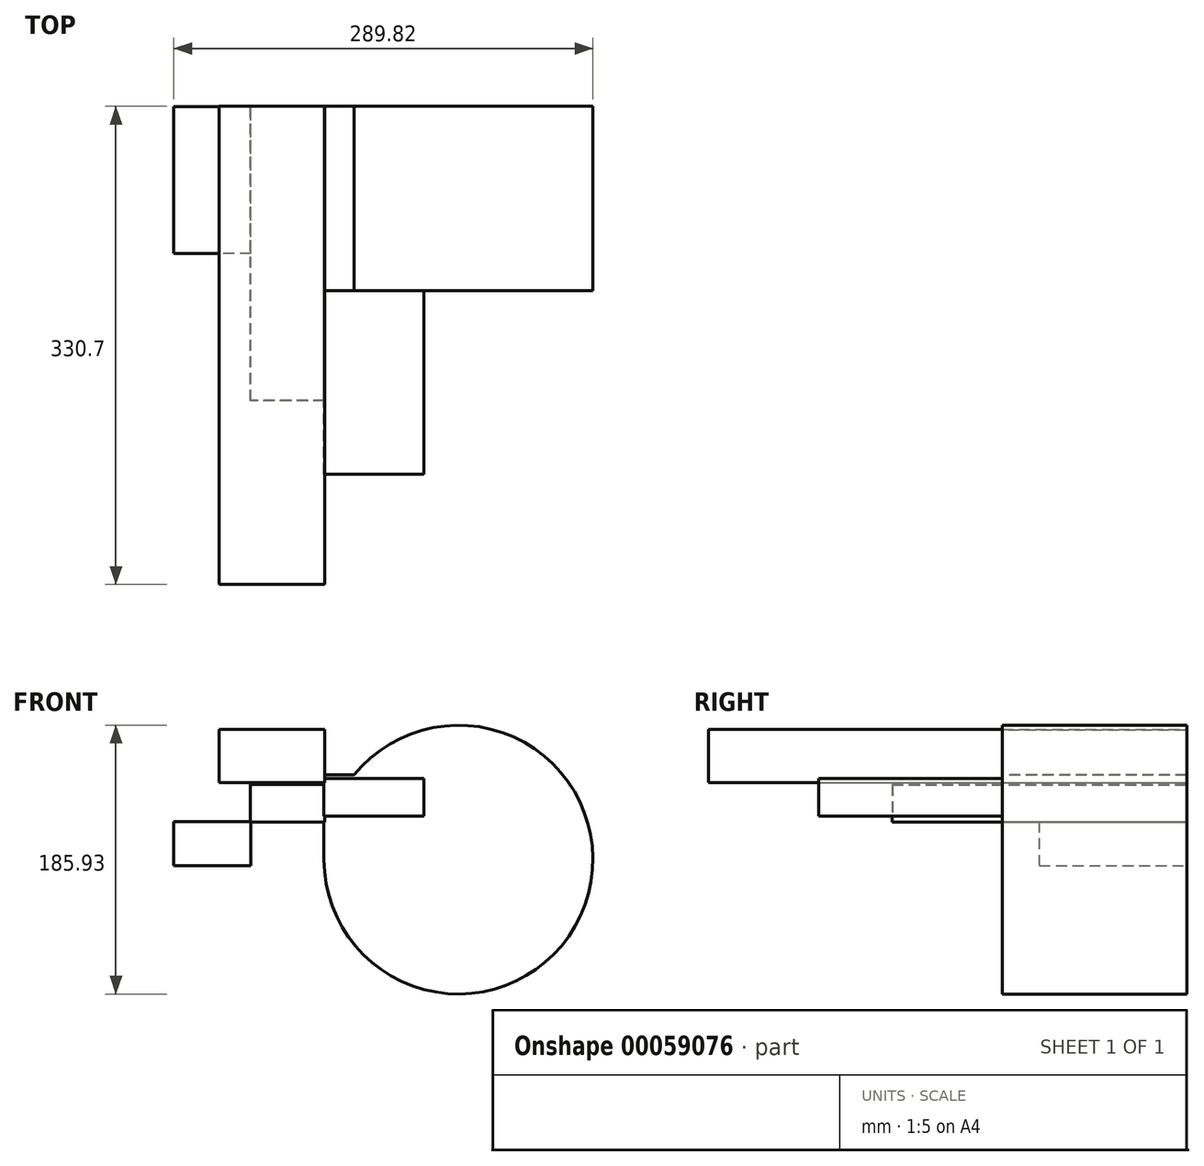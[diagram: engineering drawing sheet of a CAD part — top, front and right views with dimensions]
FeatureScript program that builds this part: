
annotation { "Feature Type Name" : "Feature", "Feature Type Description" : "" }
export const myFeature = defineFeature(function(context is Context, id is Id, definition is map)
    precondition{}
    {
        {
            var Q0;
            Q0=qCreatedBy(makeId("Front.planeOp"),FACE);
            var sketch = newSketch(context, id + "F0", { "sketchPlane" : qUnion([Q0])});
            skLineSegment(sketch, "E0.bottom", {"start": v(0, 32.05) * mm, "end": v(92.71, 32.05) * mm});
            skLineSegment(sketch, "E0.top", {"start": v(0, -26.25) * mm, "end": v(92.71, -26.25) * mm});
            skLineSegment(sketch, "E0.left", {"start": v(0, 32.05) * mm, "end": v(0, -26.25) * mm});
            skLineSegment(sketch, "E0.right", {"start": v(92.71, 32.05) * mm, "end": v(92.71, -26.25) * mm});
            skSolve(sketch);
        }
        {
            var Q0;
            Q0 = qSketchRegion(id + "F0", true);
            extrude(context, id + "F1", {"entities" : qUnion([Q0]), "depth" : 127 * mm});
        }
        {
            var Q0;
            Q0=makeQuery(id+"F1.opExtrude","CAP_FACE",FACE,{"disambiguationData":[OSD([sQuery(id+"F0.wireOp",EDGE,"E0.bottom"),sQuery(id+"F0.wireOp",EDGE,"E0.top"),sQuery(id+"F0.wireOp",EDGE,"E0.left"),sQuery(id+"F0.wireOp",EDGE,"E0.right")])],"isStart":false});
            var sketch = newSketch(context, id + "F2", { "sketchPlane" : qUnion([Q0])});
            skLineSegment(sketch, "E1.bottom", {"start": v(-7.59, 4.12) * mm, "end": v(68.61, 4.12) * mm});
            skLineSegment(sketch, "E1.top", {"start": v(-7.59, 29.52) * mm, "end": v(68.61, 29.52) * mm});
            skLineSegment(sketch, "E1.left", {"start": v(-7.59, 4.12) * mm, "end": v(-7.59, 29.52) * mm});
            skLineSegment(sketch, "E1.right", {"start": v(68.61, 4.12) * mm, "end": v(68.61, 29.52) * mm});
            skSolve(sketch);
        }
        {
            var Q0;
            {var subQ0=sQuery(id+"F2.wireOp",EDGE,"E1.right");Q0=makeQuery(id+"F2.imprint","IMPRINT",FACE,{"disambiguationData":[TD([[makeQuery(id+"F2.imprint","IMPRINT",EDGE,{"derivedFrom":subQ0}),1.0]])]});}
            extrude(context, id + "F3", {"entities" : qUnion([Q0]), "operationType" : NewBodyOperationType.ADD, "depth" : 127 * mm});
        }
        {
            var Q0;
            Q0=qCreatedBy(makeId("Top.planeOp"),FACE);
            var sketch = newSketch(context, id + "F4", { "sketchPlane" : qUnion([Q0])});
            skLineSegment(sketch, "E2.bottom", {"start": v(0, -203.2) * mm, "end": v(-50.8, -203.2) * mm});
            skLineSegment(sketch, "E2.top", {"start": v(0, 0) * mm, "end": v(-50.8, 0) * mm});
            skLineSegment(sketch, "E2.left", {"start": v(0, -203.2) * mm, "end": v(0, 0) * mm});
            skLineSegment(sketch, "E2.right", {"start": v(-50.8, -203.2) * mm, "end": v(-50.8, 0) * mm});
            skSolve(sketch);
        }
        {
            var Q0;
            Q0=makeQuery(id+"F4.imprint","IMPRINT",FACE,{"disambiguationData":[TD([[makeQuery(id+"F4.imprint","IMPRINT",EDGE,{"derivedFrom":sQuery(id+"F4.wireOp",EDGE,"E2.bottom")}),-1.0]])]});
            extrude(context, id + "F5", {"entities" : qUnion([Q0]), "operationType" : NewBodyOperationType.ADD, "depth" : 25.4 * mm});
        }
        {
            var Q0;
            Q0=makeQuery(id+"F5.opExtrude","CAP_FACE",FACE,{"disambiguationData":[OSD([sQuery(id+"F4.wireOp",EDGE,"E2.bottom"),sQuery(id+"F4.wireOp",EDGE,"E2.top"),sQuery(id+"F4.wireOp",EDGE,"E2.left"),sQuery(id+"F4.wireOp",EDGE,"E2.right")])],"isStart":true});
            var sketch = newSketch(context, id + "F6", { "sketchPlane" : qUnion([Q0])});
            skLineSegment(sketch, "E3.bottom", {"start": v(-50.8, 101.6) * mm, "end": v(-104.14, 101.6) * mm});
            skLineSegment(sketch, "E3.top", {"start": v(-50.8, 0) * mm, "end": v(-104.14, 0) * mm});
            skLineSegment(sketch, "E3.left", {"start": v(-50.8, 101.6) * mm, "end": v(-50.8, 0) * mm});
            skLineSegment(sketch, "E3.right", {"start": v(-104.14, 101.6) * mm, "end": v(-104.14, 0) * mm});
            skSolve(sketch);
        }
        {
            var Q0;
            Q0=makeQuery(id+"F6.imprint","IMPRINT",FACE,{"disambiguationData":[TD([[makeQuery(id+"F6.imprint","IMPRINT",EDGE,{"derivedFrom":sQuery(id+"F6.wireOp",EDGE,"E3.bottom")}),1.0]])]});
            extrude(context, id + "F7", {"entities" : qUnion([Q0]), "depth" : 30.48 * mm});
        }
        {
            var Q0;
            Q0=qCreatedBy(makeId("Front.planeOp"),FACE);
            var sketch = newSketch(context, id + "F8", { "sketchPlane" : qUnion([Q0])});
            skLineSegment(sketch, "E4.bottom", {"start": v(0, 63.6) * mm, "end": v(-72.47, 63.6) * mm});
            skLineSegment(sketch, "E4.top", {"start": v(0, 26.93) * mm, "end": v(-72.47, 26.93) * mm});
            skLineSegment(sketch, "E4.left", {"start": v(0, 63.6) * mm, "end": v(0, 26.93) * mm});
            skLineSegment(sketch, "E4.right", {"start": v(-72.47, 63.6) * mm, "end": v(-72.47, 26.93) * mm});
            skSolve(sketch);
        }
        {
            var Q0;
            Q0=makeQuery(id+"F8.imprint","IMPRINT",FACE,{"disambiguationData":[TD([[makeQuery(id+"F8.imprint","IMPRINT",EDGE,{"derivedFrom":sQuery(id+"F8.wireOp",EDGE,"E4.bottom")}),1.0]])]});
            extrude(context, id + "F9", {"entities" : qUnion([Q0]), "operationType" : NewBodyOperationType.ADD, "depth" : 330.2 * mm});
        }
        {
            var Q0;
            Q0=makeQuery(id+"F1.opExtrude","SWEPT_FACE",FACE,{"disambiguationData":[OSD([sQuery(id+"F0.wireOp",EDGE,"E0.top")])]});
            var Q1;
            Q1=makeQuery(id+"F1.opExtrude","SWEPT_EDGE",EDGE,{"disambiguationData":[OSD([sQuery(id+"F0.wireOp",EDGE,"E0.top"),sQuery(id+"F0.wireOp",EDGE,"E0.right")])]});
            revolve(context, id + "F10", {"operationType" : NewBodyOperationType.ADD, "entities" : qUnion([Q0]), "axis" : qUnion([Q1]), "revolveType" : RevolveType.FULL});
        }
        {
            var Q0;
            Q0=makeQuery(id+"F9.opExtrude","SWEPT_FACE",FACE,{"disambiguationData":[OSD([sQuery(id+"F8.wireOp",EDGE,"E4.top")])]});
            shell(context, id + "F11", {"entities" : qUnion([Q0]), "thickness" : 0.25 * mm, "oppositeDirection" : true});
        }
    });
